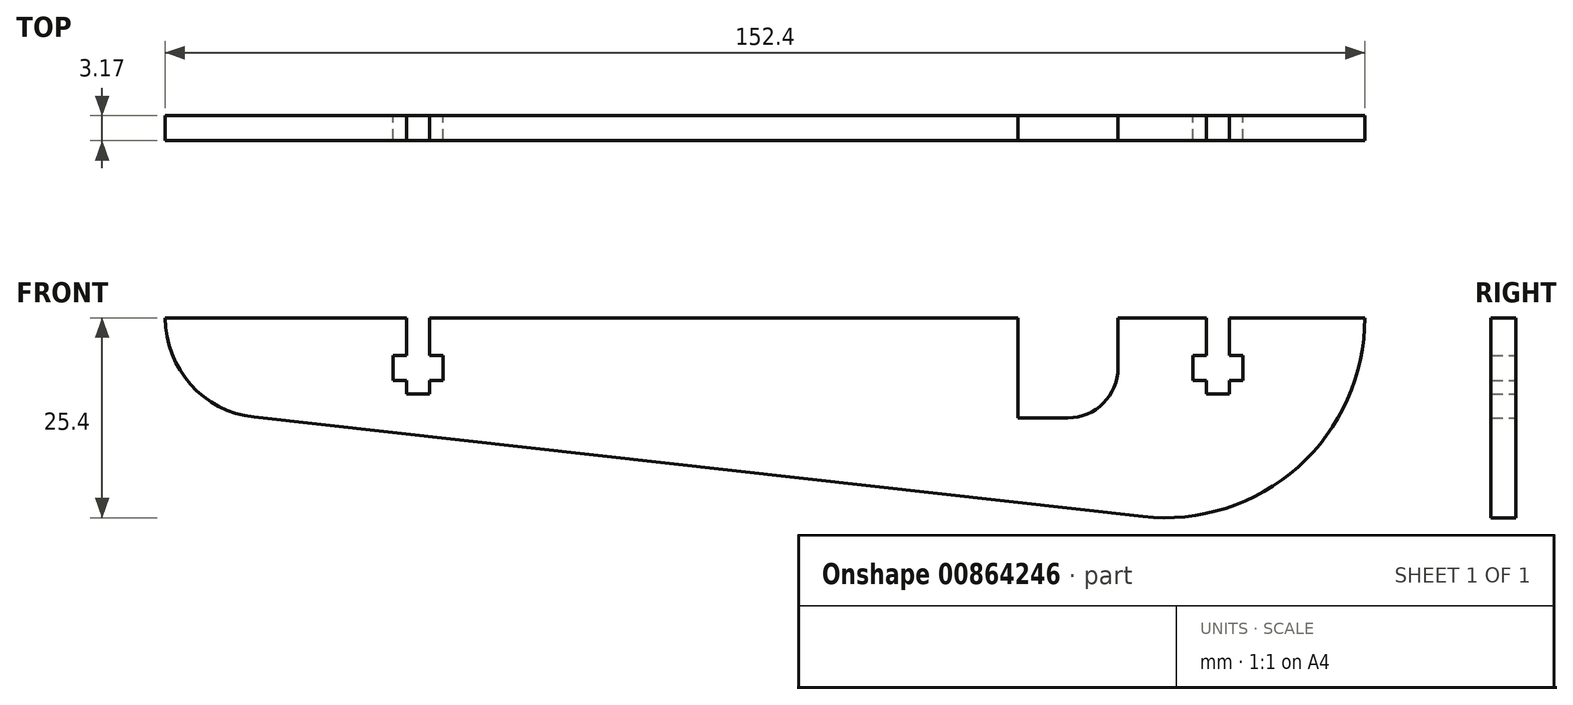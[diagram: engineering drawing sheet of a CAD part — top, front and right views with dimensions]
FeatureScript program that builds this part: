
annotation { "Feature Type Name" : "Feature", "Feature Type Description" : "" }
export const myFeature = defineFeature(function(context is Context, id is Id, definition is map)
    precondition{}
    {
        {
            var Q0;
            Q0=qCreatedBy(makeId("Front.planeOp"),FACE);
            var sketch = newSketch(context, id + "F0", { "sketchPlane" : qUnion([Q0])});
            skLineSegment(sketch, "E0", {"start": v(0, 0) * mm, "end": v(-152.4, 0) * mm});
            skCircle(sketch, "E1", {"center": v(-25.4, 0) * mm, "radius": 25.4 * mm});
            skLineSegment(sketch, "E2", {"start": v(-25.4, 0) * mm, "end": v(-25.4, -25.4) * mm});
            skCircle(sketch, "E3", {"center": v(-139.7, 0) * mm, "radius": 12.7 * mm});
            skLineSegment(sketch, "E4", {"start": v(-141.11, -12.62) * mm, "end": v(-28.22, -25.24) * mm});
            skLineSegment(sketch, "E5.bottom", {"start": v(-118.8, -9.65) * mm, "end": v(-121.72, -9.65) * mm});
            skLineSegment(sketch, "E6.bottom", {"start": v(-84.4, -4.76) * mm, "end": v(-90.75, -4.76) * mm});
            skLineSegment(sketch, "E6.top", {"start": v(-84.4, -7.94) * mm, "end": v(-90.75, -7.94) * mm});
            skLineSegment(sketch, "E6.left", {"start": v(-84.4, -4.76) * mm, "end": v(-84.4, -7.94) * mm});
            skLineSegment(sketch, "E6.right", {"start": v(-90.75, -4.76) * mm, "end": v(-90.75, -7.94) * mm});
            skPoint(sketch, "E6.middle", {"position": v(-87.58, -6.35) * mm});
            skLineSegment(sketch, "E7", {"start": v(-118.8, -9.65) * mm, "end": v(-118.8, 0) * mm});
            skLineSegment(sketch, "E8", {"start": v(-121.72, -9.65) * mm, "end": v(-121.72, 0) * mm});
            skLineSegment(sketch, "E9.bottom", {"start": v(-20.12, 0) * mm, "end": v(-17.2, 0) * mm});
            skLineSegment(sketch, "E9.top", {"start": v(-20.12, -9.65) * mm, "end": v(-17.2, -9.65) * mm});
            skLineSegment(sketch, "E9.left", {"start": v(-20.12, 0) * mm, "end": v(-20.12, -9.65) * mm});
            skLineSegment(sketch, "E9.right", {"start": v(-17.2, 0) * mm, "end": v(-17.2, -9.65) * mm});
            skLineSegment(sketch, "E10.bottom", {"start": v(-117.09, -4.76) * mm, "end": v(-123.44, -4.76) * mm});
            skLineSegment(sketch, "E10.top", {"start": v(-117.09, -7.94) * mm, "end": v(-123.44, -7.94) * mm});
            skLineSegment(sketch, "E10.left", {"start": v(-117.09, -4.76) * mm, "end": v(-117.09, -7.94) * mm});
            skLineSegment(sketch, "E10.right", {"start": v(-123.44, -4.76) * mm, "end": v(-123.44, -7.94) * mm});
            skPoint(sketch, "E10.middle", {"position": v(-120.26, -6.35) * mm});
            skLineSegment(sketch, "E11.bottom", {"start": v(-21.84, -4.76) * mm, "end": v(-15.49, -4.76) * mm});
            skLineSegment(sketch, "E11.top", {"start": v(-21.84, -7.94) * mm, "end": v(-15.49, -7.94) * mm});
            skLineSegment(sketch, "E11.left", {"start": v(-21.84, -4.76) * mm, "end": v(-21.84, -7.94) * mm});
            skLineSegment(sketch, "E11.right", {"start": v(-15.49, -4.76) * mm, "end": v(-15.49, -7.94) * mm});
            skPoint(sketch, "E11.middle", {"position": v(-18.66, -6.35) * mm});
            skLineSegment(sketch, "E12.bottom", {"start": v(-44.06, 0) * mm, "end": v(-31.36, 0) * mm});
            skLineSegment(sketch, "E12.top", {"start": v(-44.06, -12.7) * mm, "end": v(-31.36, -12.7) * mm});
            skLineSegment(sketch, "E12.left", {"start": v(-44.06, 0) * mm, "end": v(-44.06, -12.7) * mm});
            skLineSegment(sketch, "E12.right", {"start": v(-31.36, 0) * mm, "end": v(-31.36, -12.7) * mm});
            skCircle(sketch, "E13", {"center": v(-37.71, -6.35) * mm, "radius": 6.35 * mm});
            skPoint(sketch, "E13.centerSnap0", {"position": v(-37.71, -12.7) * mm});
            skSolve(sketch);
        }
        {
            var Q0;
            {var subQ11=sQuery(id+"F0.wireOp",EDGE,"E4");Q0=makeQuery(id+"F0.imprint","IMPRINT",FACE,{"disambiguationData":[TD([[makeQuery(id+"F0.imprint","IMPRINT",EDGE,{"derivedFrom":subQ11}),1.0]])]});}
            var Q1;
            Q1=makeQuery(id+"F0.imprint","IMPRINT",FACE,{"disambiguationData":[TD([[makeQuery(id+"F0.imprint","IMPRINT",EDGE,{"derivedFrom":sQuery(id+"F0.wireOp",EDGE,"E6.bottom")}),1.0]])]});
            var Q2;
            {var subQ8=sQuery(id+"F0.wireOp",EDGE,"E2");Q2=makeQuery(id+"F0.imprint","IMPRINT",FACE,{"disambiguationData":[TD([[makeQuery(id+"F0.imprint","IMPRINT",EDGE,{"derivedFrom":subQ8}),-1.0]])]});}
            var Q3;
            {var subQ8=sQuery(id+"F0.wireOp",EDGE,"E2");Q3=makeQuery(id+"F0.imprint","IMPRINT",FACE,{"disambiguationData":[TD([[makeQuery(id+"F0.imprint","IMPRINT",EDGE,{"derivedFrom":subQ8}),-1.0]])]});}
            var Q4;
            {var subQ8=sQuery(id+"F0.wireOp",EDGE,"E2");Q4=makeQuery(id+"F0.imprint","IMPRINT",FACE,{"disambiguationData":[TD([[makeQuery(id+"F0.imprint","IMPRINT",EDGE,{"derivedFrom":subQ8}),-1.0]])]});}
            var Q5;
            {var subQ0=sQuery(id+"F0.wireOp",EDGE,"E13");var subQ1=sQuery(id+"F0.wireOp",EDGE,"E12.top");var subQ2=makeQuery(id+"F0.imprint","INTERSECT",VERTEX,{"derivedFrom":[subQ1,subQ0]});Q5=makeQuery(id+"F0.imprint","IMPRINT",FACE,{"disambiguationData":[TD([[makeQuery(id+"F0.imprint","IMPRINT",EDGE,{"disambiguationData":[TD([[subQ2,-1.0]])],"derivedFrom":subQ1}),1.0]])]});}
            var Q6;
            {var subQ8=sQuery(id+"F0.wireOp",EDGE,"E2");Q6=makeQuery(id+"F0.imprint","IMPRINT",FACE,{"disambiguationData":[TD([[makeQuery(id+"F0.imprint","IMPRINT",EDGE,{"derivedFrom":subQ8}),1.0]])]});}
            var Q7;
            {var subQ0=sQuery(id+"F0.wireOp",EDGE,"E3");var subQ1=sQuery(id+"F0.wireOp",EDGE,"E0");var subQ2=makeQuery(id+"F0.imprint","INTERSECT",VERTEX,{"disambiguationData":[OD(0.0)],"derivedFrom":[subQ1,subQ0]});Q7=makeQuery(id+"F0.imprint","IMPRINT",FACE,{"disambiguationData":[TD([[makeQuery(id+"F0.imprint","IMPRINT",EDGE,{"disambiguationData":[TD([[subQ2,1.0]])],"derivedFrom":subQ1}),1.0]])]});}
            extrude(context, id + "F1", {"entities" : qUnion([Q0, Q1, Q2, Q3, Q4, Q5, Q6, Q7]), "depth" : 3.17 * mm, "offsetDistance" : 25.4 * mm});
        }
    });
